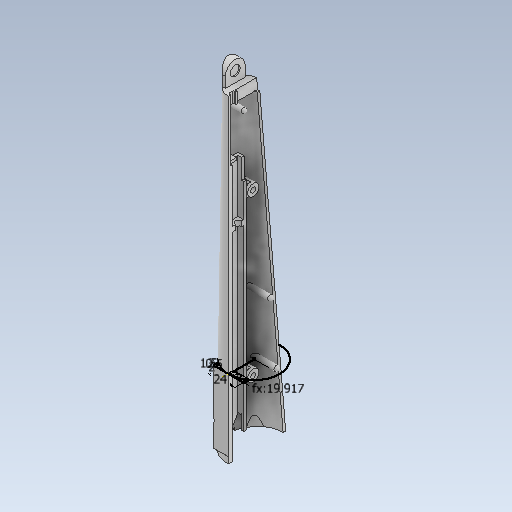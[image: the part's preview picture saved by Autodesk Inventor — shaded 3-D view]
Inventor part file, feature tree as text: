
AUTODESK INVENTOR PART (.ipt)
format: ipt  version: 2021 (Build 250183000, 183)  size: 919,552 bytes
history: native  units: mm
features: sketch x37, extrude x32, plane x16, fillet x5, hole x3, loft x2, revolve x2, other x1, thread x1
ambient origin geometry x8: Origin, YZ Plane, XZ Plane, XY Plane, X Axis, Y Axis, Z Axis, Center Point
bodies: Body1 (feature_tree)
feature tree (99):
  other  "Sólido1"
  plane  "Plano de trabajo1"
  plane  "Plano de trabajo2"
  plane  "Plano de trabajo4"
  plane  "Plano de trabajo5"
  plane  "Plano de trabajo6"
  sketch  "Boceto1"  dims[d1=250.0mm d2=0.0mm d3=-80.0mm d4=-110.0mm]
  sketch  "Boceto2"  dims[d5=-140.0mm d7=-0.0mm d8=2.0mm]
  sketch  "Boceto3"  dims[d9=140.0mm d10=250.0mm]
  sketch  "Boceto4"  dims[d11=24.0mm d22=0.0mm d23=90.0deg d24=0.0mm d25=90.0deg]
  sketch  "Boceto6"  dims[d44=45.0mm d49=29.11157mm]
  sketch  "Boceto7"  dims[d50=29.11157mm d53=29.11157mm]
  loft  "Solevación1"
  fillet  "Empalme2"  [1 undecoded]
  extrude  "Extrusión1"  TaperAngle=0.0deg  [1 undecoded]
  fillet  "Empalme5"  Radius=2.0mm
  plane  "Plano de trabajo7"
  extrude  "Extrusión2"  Depth=250.0mm
  plane  "Plano de trabajo8"
  plane  "Plano de trabajo9"
  loft  "Solevación9"
  plane  "Plano de trabajo10"
  extrude  "Extrusión3"  Depth=29.11157mm
  plane  "Plano de trabajo11"
  revolve  "Revolución1"  [1 undecoded]
  revolve  "Revolución2"  [1 undecoded]
  extrude  "Extrusión4"  Depth=32.5mm
  plane  "Plano de trabajo12"
  extrude  "Extrusión5"  Depth=44.747934mm
  plane  "Plano de trabajo13"
  plane  "Plano de trabajo14"
  extrude  "Extrusión6"  Depth=42.747934mm
  extrude  "Extrusión7"  Depth=42.747934mm
  extrude  "Extrusión8"  Depth=13.0mm
  extrude  "Extrusión11"  Depth=7.75mm
  extrude  "Extrusión9"  Depth=7.75mm
  extrude  "Extrusión10"  Depth=16.0mm
  extrude  "Extrusión12"  Depth=12.0mm
  sketch  "Boceto30"  dims[d160=-19.75mm d161=0.0mm d163=0.0mm d164=2.0mm]
  extrude  "Extrusión13"  Depth=7.75mm
  extrude  "Extrusión14"  Depth=7.75mm
  extrude  "Extrusión15"  TaperAngle=0.0deg  [1 undecoded]
  hole  "Agujero1"  [1 undecoded]
  thread  "Rosca1"  [1 undecoded]
  extrude  "Extrusión16"  Depth=2.0mm
  plane  "Plano de trabajo16"
  extrude  "Extrusión17"  TaperAngle=0.0deg  [1 undecoded]
  extrude  "Extrusión18"  TaperAngle=0.0deg  [1 undecoded]
  fillet  "Empalme6"  [1 undecoded]
  fillet  "Empalme7"  Radius=2.0mm
  plane  "Plano de trabajo17"
  sketch  "Boceto46"  dims[d185=2.0mm d187=1.0mm]
  hole  "Agujero2"  [1 undecoded]
  hole  "Agujero3"  [1 undecoded]
  extrude  "Extrusión21"  [1 undecoded]
  plane  "Plano de trabajo19"
  sketch  "Boceto50"  dims[d193=0.25mm d194=90.0deg]
  extrude  "Extrusión34"  Depth=0.75mm
  extrude  "Extrusión35"  Depth=1.0mm
  extrude  "Extrusión37"  Depth=17.453293mm
  sketch  "Boceto44"  dims[d181=0.75mm d182=0.25mm]
  extrude  "Extrusión23"  Depth=0.75mm
  sketch  "Boceto47"  dims[d189=3.0mm d190=2.0mm]
  extrude  "Extrusión22"  Depth=0.25mm
  sketch  "Boceto45"  dims[d183=1.0mm d184=0.25mm]
  extrude  "Extrusión32"  Depth=0.25mm
  extrude  "Extrusión30"  Depth=2.0mm
  extrude  "Extrusión31"  Depth=2.0mm
  extrude  "Extrusión33"  Depth=2.0mm
  extrude  "Extrusión28"  TaperAngle=90.0deg  [1 undecoded]
  sketch  "Boceto49"  dims[d191=2.0mm d192=0.25mm]
  extrude  "Extrusión24"  [1 undecoded]
  extrude  "Extrusión36"  Depth=2.0mm
  extrude  "Extrusión25"  Depth=2.0mm
  fillet  "Empalme8"  Radius=9.0mm
  sketch  "Boceto9"  dims[d59=29.11157mm d61=29.11157mm]
  sketch  "Boceto10"  dims[d65=22.5mm d66=32.5mm]
  sketch  "Boceto15"  dims[d67=22.5mm d90=44.747934mm]
  sketch  "Boceto16"  dims[d91=42.747934mm d93=42.747934mm]
  sketch  "Boceto17"  dims[d96=0.0mm d97=90.0deg d98=0.0mm d99=90.0deg d100=0.0mm d101=90.0deg d102=0.0mm d103=90.0deg d112=42.747934mm]
  sketch  "Boceto18"  dims[d115=5.0mm d120=13.0mm]
  sketch  "Boceto19"  dims[d121=6.5mm d124=7.75mm]
  sketch  "Boceto20"  dims[d125=7.75mm d126=7.75mm]
  sketch  "Boceto21"  dims[d127=7.75mm d130=16.0mm]
  sketch  "Boceto22"  dims[d131=0.0mm d132=12.0mm]
  sketch  "Boceto24"  dims[d133=12.0mm d134=7.75mm]
  sketch  "Boceto25"  dims[d135=6.5mm d136=7.75mm]
  sketch  "Boceto26"  dims[d137=15.0mm d138=0.0mm]
  sketch  "Boceto27"  dims[d146=-8.5mm d147=30.0mm d148=2.0mm]
  sketch  "Boceto28"  dims[d149=25.12mm d150=2.0mm]
  sketch  "Boceto29"  dims[d151=10.357mm d156=0.0mm d157=90.0deg d158=0.0mm d159=90.0deg]
  sketch  "Boceto31"  dims[d165=15.0mm d166=4.0mm]
  sketch  "Boceto36"  dims[d167=30.0mm d168=12.0mm]
  sketch  "Boceto37"  dims[d169=0.0mm d170=-7.25mm]
  sketch  "Boceto38"  dims[d171=4.5mm d172=0.75mm]
  sketch  "Boceto39"  dims[d173=2.5mm d174=1.0mm]
  sketch  "Boceto40"  dims[d176=11.0mm d177=17.453293mm]
  sketch  "Boceto41"  dims[d179=2.939597mm d180=0.75mm]
  sketch  "Boceto51"  dims[d196=4.381635mm d197=0.0mm d198=-48.35mm d199=12.0mm d200=20.0mm d201=9.0mm d202=9.0mm d203=2.0mm d204=201.65mm d205=0.0mm d206=0.5mm d207=0.25mm d208=-7.5mm d209=100.0mm d210=0.0mm d211=35.0mm d212=0.0mm d213=210.0mm d214=0.0mm d215=2.0mm d216=1.059493mm d217=6.5mm d218=1.059493mm d219=5.0mm d220=2.0mm d221=0.0mm d222=2.0mm d223=6.5mm d224=1.059493mm d225=5.0mm d226=4.85mm d227=2.0mm d228=0.0mm d229=6.0mm d230=10.0mm d231=3.0mm d232=11.0mm d233=10.5mm d235=30.0deg d236=4.75mm d237=0.0mm d238=-17.0mm d239=100.0mm d240=0.0mm d241=6.5mm d242=1.65mm d243=3.3mm d244=15.6mm d245=2.0mm d247=16.0mm d248=2.0mm d249=0.0mm d250=4.5mm d251=0.75mm d252=2.5mm d253=1.0mm d254=11.0mm d255=17.453293mm d256=2.939597mm d257=0.75mm d258=0.75mm d259=0.25mm d260=1.0mm d261=0.25mm d262=2.0mm d263=1.0mm d264=3.0mm d265=2.0mm d266=2.0mm d267=0.25mm d268=0.25mm d269=40.0mm d270=1.0mm d271=1.0mm d272=7.75mm d273=0.5mm d274=8.5mm d275=90.0deg d276=0.0mm d277=17.75mm d280=22.5mm d281=2.0mm d282=0.0mm d283=0.0mm d292=2.0mm d293=0.0mm d296=3.5mm d297=0.0mm d299=4.0mm d300=3.708mm d301=3.023mm d302=2.0mm d303=14.3117mm d304=16.0mm d305=0.0mm d306=16.0mm d307=0.0mm d314=6.0mm d315=19.2mm d316=6.0mm d317=19.2mm d318=13.0mm d320=6.0mm d321=19.2mm d322=13.0mm d323=6.0mm d324=19.2mm d325=13.0mm d326=7.0mm d332=10.0mm d333=0.0mm d335=-41.6mm d336=4.0mm d337=1.0mm d338=9.0mm d339=4.0mm d340=1.0mm d341=9.0mm d342=4.0mm d343=5.2mm d344=4.0mm d345=0.0mm d346=15.0mm d347=5.0mm d349=5.0mm d351=0.0mm d352=45.0mm d354=10.0mm d355=10.0mm d356=0.0mm d357=15.0mm d358=0.0mm d359=2.0mm d363=50.4125mm d376=14.159493mm d377=2.0mm d379=2.0mm d380=11.25mm d381=90.0mm d382=290.0mm d383=14.059493mm d384=100.825mm d390=30.940507mm d391=2.0mm d392=100.825mm d393=14.790546mm d394=2.0mm d395=3.0mm d396=6.0mm d397=4.0mm d398=4.0mm d399=4.0mm d400=8.128453mm d401=12.0mm d402=4.45mm d403=2.5mm d404=1.65mm d405=1.65mm d406=1.0mm d407=2.0mm d408=2.0mm d409=0.0mm d411=50.4125mm d412=6.0mm d418=13.059493mm d419=6.5mm d420=6.5mm d421=50.4125mm d422=126.03125mm d423=0.0mm d424=15.0mm d425=5.0mm d426=5.0mm d427=0.0mm d428=45.0mm d429=10.0mm d430=2.0mm d431=4.0mm d432=6.0mm d433=8.0mm d434=2.0mm d435=90.0deg d436=20.0mm d437=0.0mm d438=4.0mm d439=6.0mm d440=8.0mm d441=2.0mm d442=90.0deg d443=20.0mm d444=0.0mm d446=10.0mm d447=3.0mm d448=11.5mm d450=9.0mm d451=9.0mm d452=90.0mm d453=750.0mm d454=22.5mm d455=43.0mm d456=44.0mm d457=14.159493mm d458=11.25mm d459=2.0mm d460=0.0mm d461=22.5mm d462=43.0mm d463=7.059493mm d464=3.0mm d465=6.0mm d466=3.0mm d467=6.0mm d468=180.0mm d469=0.0mm d470=180.0mm d471=0.0mm d472=4.5mm d473=10.0mm d474=0.0mm d475=7.0mm d476=0.0mm d481=14.059493mm d482=250.0mm d483=2.0mm d484=0.0mm d485=4.0mm d486=4.0mm d487=4.0mm d490=6.0mm d491=0.0mm d492=4.0mm d493=4.0mm d494=0.0mm d495=0.0mm d496=0.0mm d497=0.0mm d498=4.5mm d499=11.0mm d500=0.0mm d501=2.0mm d502=0.0mm d503=61.5mm d504=19.917mm d508=24.0mm d509=56.5mm d510=0.0mm d511=1.5mm d512=2.0mm d513=2.0mm d514=52.5mm d515=0.0mm d516=35.0mm d517=3.0mm d518=150.0deg d520=61.5mm d521=2.0mm d522=2.0mm d523=0.0mm d524=0.5mm d525=25.0mm d526=0.0mm d527=0.5mm d528=0.872665mm d529=0.5mm d530=0.872665mm]
note: 15 required parameter values undecoded (feature->parameter linkage not recoverable at this tier; creation-order binding heuristic only, values carry confidence <= 0.55)